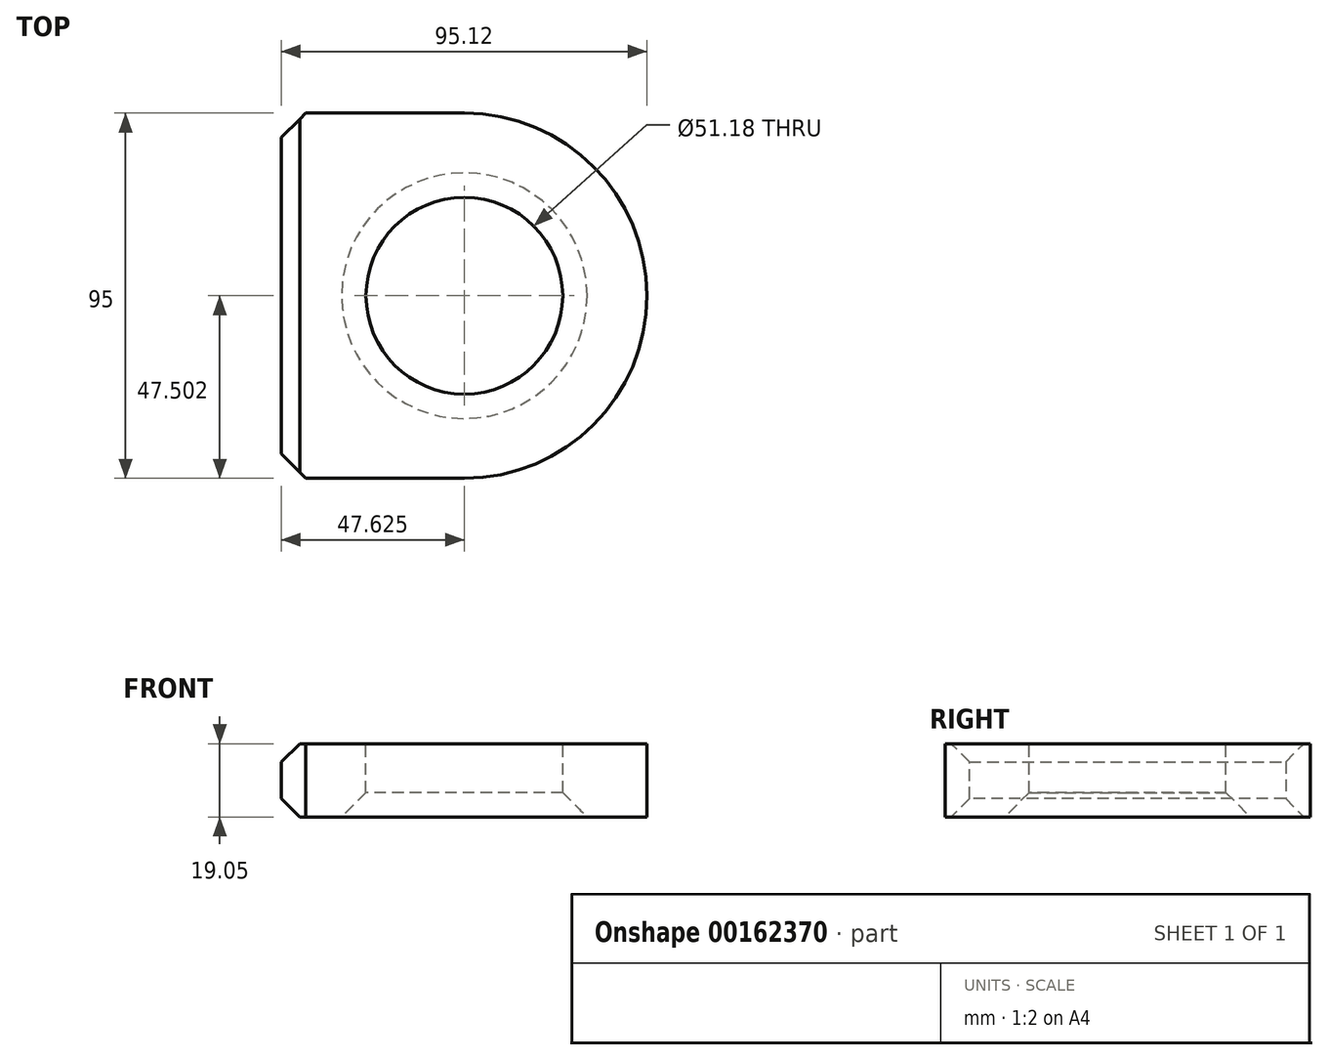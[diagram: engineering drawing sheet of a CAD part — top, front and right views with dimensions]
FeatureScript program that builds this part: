
annotation { "Feature Type Name" : "Feature", "Feature Type Description" : "" }
export const myFeature = defineFeature(function(context is Context, id is Id, definition is map)
    precondition{}
    {
        {
            var Q0;
            Q0=qCreatedBy(makeId("Top.planeOp"),FACE);
            var sketch = newSketch(context, id + "F0", { "sketchPlane" : qUnion([Q0])});
            skLineSegment(sketch, "E0.bottom", {"start": v(0, 0) * mm, "end": v(47.62, 0) * mm});
            skLineSegment(sketch, "E0.top", {"start": v(0, -95) * mm, "end": v(47.62, -95) * mm});
            skLineSegment(sketch, "E0.left", {"start": v(0, 0) * mm, "end": v(0, -95) * mm});
            skArc(sketch, "E1", {"start": v(47.62, -95) * mm, "mid": v(95.12, -47.5) * mm, "end": v(47.63, 0) * mm});
            skSolve(sketch);
        }
        {
            var Q0;
            Q0 = qSketchRegion(id + "F0", true);
            extrude(context, id + "F1", {"entities" : qUnion([Q0]), "depth" : 19.05 * mm});
        }
        {
            var Q0;
            Q0=makeQuery(id+"F1.opExtrude","CAP_FACE",FACE,{"disambiguationData":[OSD([sQuery(id+"F0.wireOp",EDGE,"E0.bottom"),sQuery(id+"F0.wireOp",EDGE,"E0.top"),sQuery(id+"F0.wireOp",EDGE,"E0.left"),sQuery(id+"F0.wireOp",EDGE,"E1")])],"isStart":false});
            var sketch = newSketch(context, id + "F2", { "sketchPlane" : qUnion([Q0])});
            skCircle(sketch, "E2", {"center": v(47.62, -47.5) * mm, "radius": 25.6 * mm});
            skSolve(sketch);
        }
        {
            var Q0;
            Q0 = qSketchRegion(id + "F2", true);
            extrude(context, id + "F3", {"entities" : qUnion([Q0]), "operationType" : NewBodyOperationType.REMOVE, "endBound" : BoundingType.THROUGH_ALL, "oppositeDirection" : true, "depth" : 25.4 * mm});
        }
        {
            var Q0;
            Q0=makeQuery(id+"F1.opExtrude","SWEPT_EDGE",EDGE,{"disambiguationData":[OSD([sQuery(id+"F0.wireOp",EDGE,"E0.bottom"),sQuery(id+"F0.wireOp",EDGE,"E0.left")])]});
            var Q1;
            Q1=makeQuery(id+"F1.opExtrude","SWEPT_EDGE",EDGE,{"disambiguationData":[OSD([sQuery(id+"F0.wireOp",EDGE,"E0.top"),sQuery(id+"F0.wireOp",EDGE,"E0.left")])]});
            var Q2;
            Q2=makeQuery(id+"F3.boolean.opBoolean","COPY",EDGE,{"derivedFrom":makeQuery(id+"F3.opExtrude","CAP_EDGE",EDGE,{"disambiguationData":[OSD([sQuery(id+"F2.wireOp",EDGE,"E2")])],"isStart":true})});
            var Q3;
            Q3=makeQuery(id+"F3.boolean.opBoolean","INTERSECT",EDGE,{"derivedFrom":[makeQuery(id+"F1.opExtrude","CAP_FACE",FACE,{"disambiguationData":[OSD([sQuery(id+"F0.wireOp",EDGE,"E0.bottom"),sQuery(id+"F0.wireOp",EDGE,"E0.top"),sQuery(id+"F0.wireOp",EDGE,"E0.left"),sQuery(id+"F0.wireOp",EDGE,"E1")])],"isStart":true}),makeQuery(id+"F3.opExtrude","SWEPT_FACE",FACE,{"disambiguationData":[OSD([sQuery(id+"F2.wireOp",EDGE,"E2")])]})]});
            chamfer(context, id + "F4", {"entities" : qUnion([Q0, Q1, Q2, Q3]), "width" : 6.35 * mm, "tangentPropagation" : true});
        }
        {
            var Q0;
            Q0=makeQuery(id+"F1.opExtrude","CAP_EDGE",EDGE,{"disambiguationData":[OSD([sQuery(id+"F0.wireOp",EDGE,"E0.left")])],"isStart":false});
            var Q1;
            Q1=makeQuery(id+"F1.opExtrude","CAP_EDGE",EDGE,{"disambiguationData":[OSD([sQuery(id+"F0.wireOp",EDGE,"E0.left")])],"isStart":true});
            chamfer(context, id + "F5", {"entities" : qUnion([Q0, Q1]), "width" : 4.76 * mm, "tangentPropagation" : true});
        }
    });
